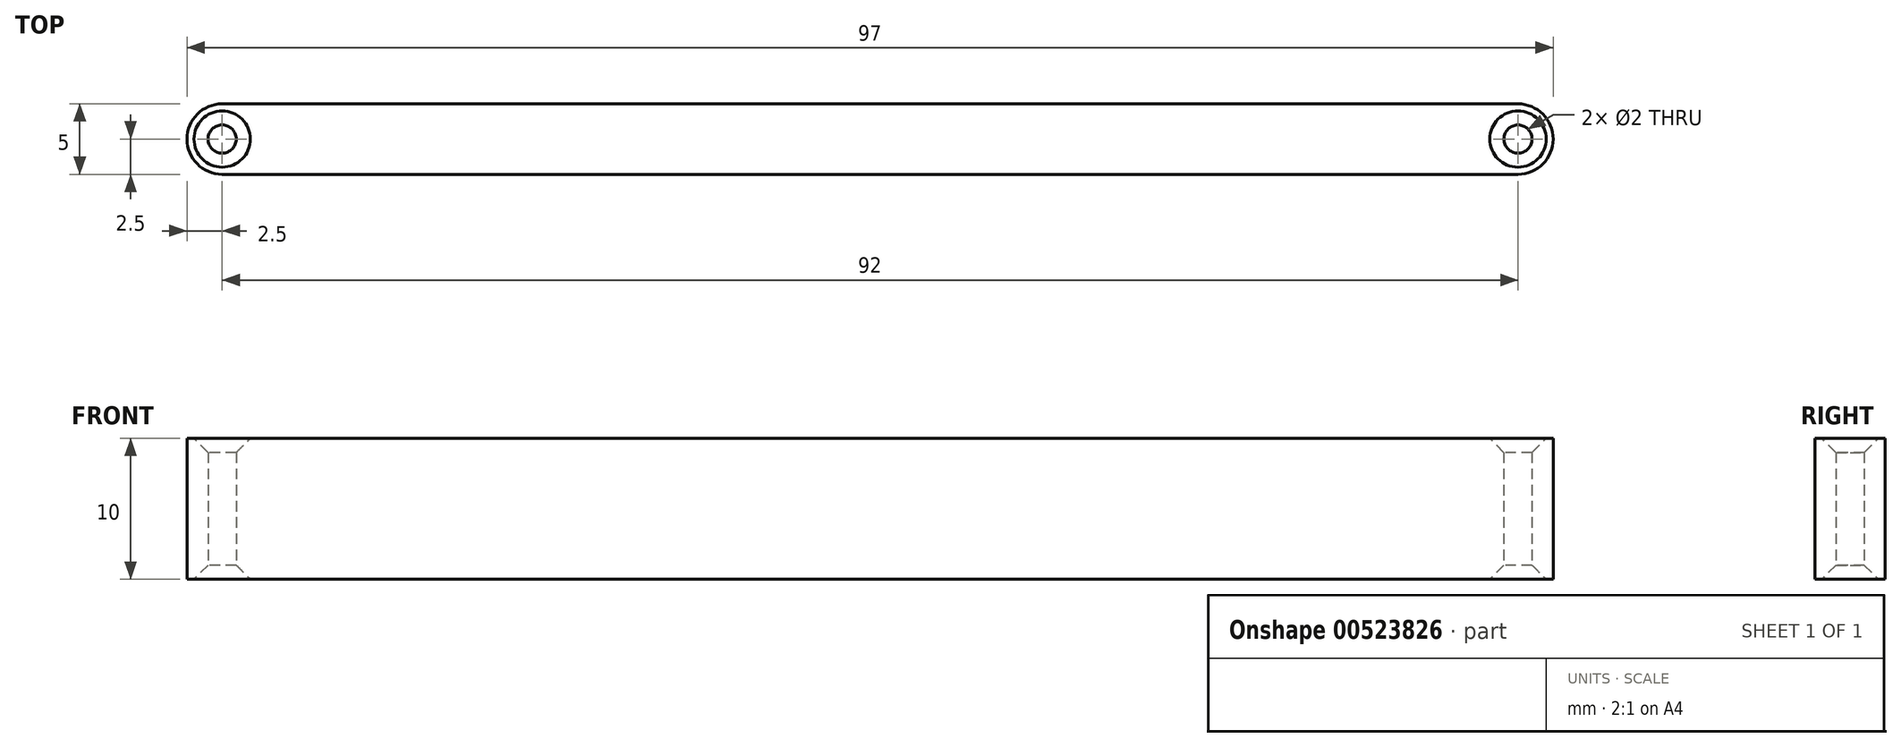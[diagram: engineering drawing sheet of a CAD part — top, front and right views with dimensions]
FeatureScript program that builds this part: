
annotation { "Feature Type Name" : "Feature", "Feature Type Description" : "" }
export const myFeature = defineFeature(function(context is Context, id is Id, definition is map)
    precondition{}
    {
        {
            var Q0;
            Q0=qCreatedBy(makeId("Top.planeOp"),FACE);
            var sketch = newSketch(context, id + "F0", { "sketchPlane" : qUnion([Q0])});
            skLineSegment(sketch, "E0.bottom", {"start": v(48.5, -2.5) * mm, "end": v(-48.5, -2.5) * mm});
            skLineSegment(sketch, "E0.top", {"start": v(48.5, 2.5) * mm, "end": v(-48.5, 2.5) * mm});
            skLineSegment(sketch, "E0.left", {"start": v(48.5, -2.5) * mm, "end": v(48.5, 2.5) * mm});
            skLineSegment(sketch, "E0.right", {"start": v(-48.5, -2.5) * mm, "end": v(-48.5, 2.5) * mm});
            skPoint(sketch, "E0.middle", {"position": v(0, 0) * mm});
            skCircle(sketch, "E1", {"center": v(-46, 0) * mm, "radius": 1 * mm});
            skPoint(sketch, "E1.centerSnap0", {"position": v(-48.5, 0) * mm});
            skCircle(sketch, "E2", {"center": v(46, 0) * mm, "radius": 1 * mm});
            skPoint(sketch, "E2.centerSnap0", {"position": v(48.5, 0) * mm});
            skLineSegment(sketch, "E3", {"start": v(-46, 0) * mm, "end": v(-48.5, 0) * mm, "construction": true});
            skLineSegment(sketch, "E4", {"start": v(46, 0) * mm, "end": v(48.5, 0) * mm, "construction": true});
            skSolve(sketch);
        }
        {
            var Q0;
            Q0=makeQuery(id+"F0.imprint","IMPRINT",FACE,{"disambiguationData":[TD([[makeQuery(id+"F0.imprint","IMPRINT",EDGE,{"derivedFrom":sQuery(id+"F0.wireOp",EDGE,"E0.bottom")}),-1.0]])]});
            extrude(context, id + "F1", {"entities" : qUnion([Q0]), "depth" : 10 * mm, "offsetDistance" : 25 * mm});
        }
        {
            var Q0;
            Q0=makeQuery(id+"F1.opExtrude","SWEPT_EDGE",EDGE,{"disambiguationData":[OSD([sQuery(id+"F0.wireOp",EDGE,"E0.top"),sQuery(id+"F0.wireOp",EDGE,"E0.left")])]});
            var Q1;
            Q1=makeQuery(id+"F1.opExtrude","SWEPT_EDGE",EDGE,{"disambiguationData":[OSD([sQuery(id+"F0.wireOp",EDGE,"E0.bottom"),sQuery(id+"F0.wireOp",EDGE,"E0.left")])]});
            var Q2;
            Q2=makeQuery(id+"F1.opExtrude","SWEPT_EDGE",EDGE,{"disambiguationData":[OSD([sQuery(id+"F0.wireOp",EDGE,"E0.top"),sQuery(id+"F0.wireOp",EDGE,"E0.right")])]});
            var Q3;
            Q3=makeQuery(id+"F1.opExtrude","SWEPT_EDGE",EDGE,{"disambiguationData":[OSD([sQuery(id+"F0.wireOp",EDGE,"E0.bottom"),sQuery(id+"F0.wireOp",EDGE,"E0.right")])]});
            fillet(context, id + "F2", {"entities" : qUnion([Q0, Q1, Q2, Q3]), "radius" : 2.5 * mm, "tangentPropagation" : true, "allowEdgeOverflow" : false});
        }
        {
            var Q0;
            Q0=makeQuery(id+"F1.opExtrude","CAP_EDGE",EDGE,{"disambiguationData":[OSD([sQuery(id+"F0.wireOp",EDGE,"E1")])],"isStart":false});
            var Q1;
            Q1=makeQuery(id+"F1.opExtrude","CAP_EDGE",EDGE,{"disambiguationData":[OSD([sQuery(id+"F0.wireOp",EDGE,"E2")])],"isStart":false});
            var Q2;
            Q2=makeQuery(id+"F1.opExtrude","CAP_EDGE",EDGE,{"disambiguationData":[OSD([sQuery(id+"F0.wireOp",EDGE,"E2")])],"isStart":true});
            var Q3;
            Q3=makeQuery(id+"F1.opExtrude","CAP_EDGE",EDGE,{"disambiguationData":[OSD([sQuery(id+"F0.wireOp",EDGE,"E1")])],"isStart":true});
            chamfer(context, id + "F3", {"entities" : qUnion([Q0, Q1, Q2, Q3]), "width" : 1 * mm, "tangentPropagation" : true});
        }
    });
